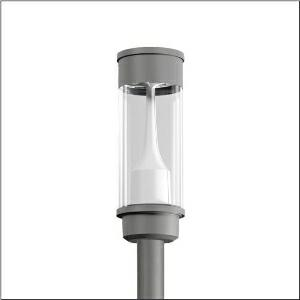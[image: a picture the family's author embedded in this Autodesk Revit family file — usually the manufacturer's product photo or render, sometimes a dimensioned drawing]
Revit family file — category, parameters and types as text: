
# Revit family: litepole_iq___p1_0a_5xa5415bf14h_51c2
name_source: partatom
category: Lighting Fixtures
units: mm (PartAtom-declared; Revit-internal decimal feet)

## family parameters
Cut with Voids When Loaded = No
Host = Face
Light Source = No
Part Type = Normal
Room Calculation Point = No
Round Connector Dimension = Use Diameter
Shared = No

## types (1)
- --- (1 x LED, 1510 lm, 12.9 W, 2200K)
    Apparent Load = 13 VA
    CIE Flux Codes = 32 61 90 93 100
    Color Rendering = 70
    Color Temperature = 2200K
    Default Elevation = 1800 mm
    Description = Litepole iQ, mast luminaire, Module 540 iQ-SR, primary light control with 3 zone facetted reflector, of plastic, silver coated, highly specular, structured, primary optical cover: cover, of PMMA, transparent, partly coated, light distribution: P1.0a, light emission: direct distribution, primary light characteristic: strongly asymmetric, installation type: post-top, LED, High Power LED, rated luminous flux: 1.510lm, luminous efficacy: 117lm/W, light colour: 722, colour temperature: 2200K, control gear: iQ Street-Remote, control: optimised constant luminous flux control (CLO 2.0), Desk-Remote (wireless, voltage-free reading and setting of iQ features in the workshop via application-optimized NFC function/RFID function), Light-Fading, Smart-Wire, Night-Set, Lumen-Switch, Temp-Guard, Auto-Match, Street-Remote, pre-setting: logarithmic dimming characteristic, with terminal, 6-pole, max. 2.5mm², mains connection: 230..240V, AC, 50/60Hz, start of lifetime: 13W, end of service life: 13W, reduction: 6W, luminaire housing, upper part, of glass-fibre reinforced polyester, coated, Siteco® metallic grey (DB 702S), diameter: 210mm, height: 590mm, spigot size: d x l = 76 x 70mm (post-top) | with reducer (optional accessory) 60 x 70mm, mounting height: 3..5m, post-top mast mounting element, of diecast aluminium, coated, Siteco® metallic grey (DB 702S), Module 540 iQ-SR, traffic white (RAL 9016), equipment: standard, protection rating (complete): IP65, insulation class (complete): insulation class II (safety insulation), certification: CE, ENEC, VDE, packaging unit: 1 piece

Light Distribution: P1.0a
    Height = 590 mm
    Lamp = 1 x LED
    Lamp Light Flux = 1510 lm
    Lamp Power = 12.9 W
    Lamp count = 1
    Length = 220 mm
    Luminous efficacy = 117 lm/W
    Manufacturer = Siteco
    ModVariant = No
    Model = 5XA5415BF14H
    Number of Poles = 1
    OnlyDefault = Yes
    Power Factor = 1
    Product Name = Litepole iQ | P1.0a
    Product group = mast luminaire | pylon top
    ProductGroupID = 6100
    Protection Class = Protection class II
    Protection Degree = IP 65
    RLX_Detail_Level = 1
    RLX_Emergency_Light_Flux = 0 lm
    RLX_Emergency_Type = 0
    RLX_Emergency_Type_DB = No
    RlxData = <blob elided: 64369 chars, md5=69f6ff3f>
    Socket = socket
    Standby Power = 0 W
    System Light Flux = 1510 lm
    System Power = 13 W
    Type Comments = factory setting: luminous flux: 100 % | dim-lin: 254 | 516 mA
    Type Image = l_1006025.jpg
    URL = http://relux.com
    VarID = @adj_158239
    Voltage = 0 V
    Weight = 0.00 kg
    Width = 0 mm  [stored 0 ft]

note: [stored X ft] marks values corroborated as IEEE doubles in the binary element streams (Revit-internal decimal feet)

## geometry (parser evidence)
native form markers: Blend x4, Sweep x12
no freeform markers — native parametric forms only
